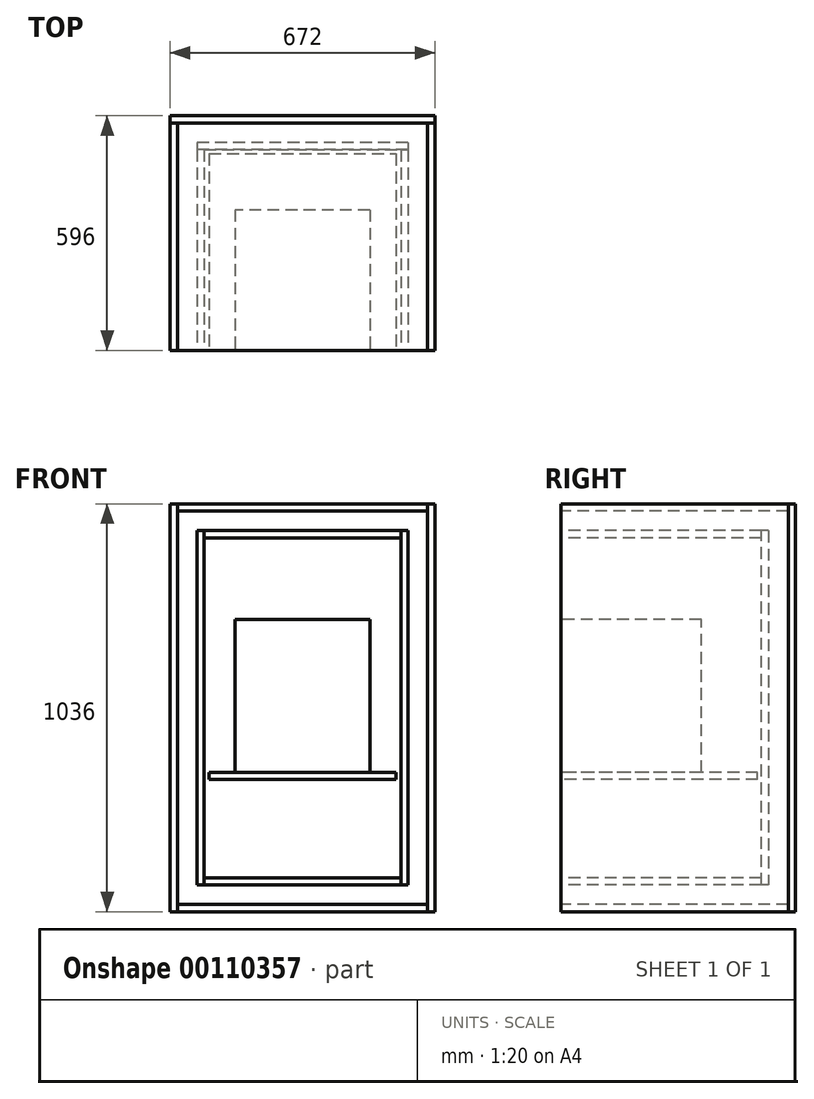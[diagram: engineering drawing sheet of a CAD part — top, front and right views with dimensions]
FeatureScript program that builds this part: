
annotation { "Feature Type Name" : "Feature", "Feature Type Description" : "" }
export const myFeature = defineFeature(function(context is Context, id is Id, definition is map)
    precondition{}
    {
        {
            var Q0;
            Q0=qCreatedBy(makeId("Front.planeOp"),FACE);
            var sketch = newSketch(context, id + "F0", { "sketchPlane" : qUnion([Q0])});
            skLineSegment(sketch, "E0.bottom", {"start": v(250, 0) * mm, "end": v(-250, 0) * mm});
            skLineSegment(sketch, "E0.top", {"start": v(250, 18) * mm, "end": v(-250, 18) * mm});
            skLineSegment(sketch, "E0.left", {"start": v(250, 0) * mm, "end": v(250, 18) * mm});
            skLineSegment(sketch, "E0.right", {"start": v(-250, 0) * mm, "end": v(-250, 18) * mm});
            skPoint(sketch, "E0.middle", {"position": v(0, 9) * mm});
            skLineSegment(sketch, "E1.bottom", {"start": v(-237.5, 268) * mm, "end": v(237.5, 268) * mm});
            skLineSegment(sketch, "E1.top", {"start": v(-237.5, 286) * mm, "end": v(237.5, 286) * mm});
            skLineSegment(sketch, "E1.left", {"start": v(-237.5, 268) * mm, "end": v(-237.5, 286) * mm});
            skLineSegment(sketch, "E1.right", {"start": v(237.5, 268) * mm, "end": v(237.5, 286) * mm});
            skLineSegment(sketch, "E2.bottom", {"start": v(250, 0) * mm, "end": v(268, 0) * mm});
            skLineSegment(sketch, "E2.top", {"start": v(250, 900) * mm, "end": v(268, 900) * mm});
            skLineSegment(sketch, "E2.left", {"start": v(250, 0) * mm, "end": v(250, 900) * mm});
            skLineSegment(sketch, "E2.right", {"start": v(268, 0) * mm, "end": v(268, 900) * mm});
            skLineSegment(sketch, "E3.MirrorCS", {"start": v(-250, 0) * mm, "end": v(-268, 0) * mm});
            skLineSegment(sketch, "E4.MirrorCS", {"start": v(-268, 0) * mm, "end": v(-268, 900) * mm});
            skLineSegment(sketch, "E5.MirrorCS", {"start": v(-250, 0) * mm, "end": v(-250, 900) * mm});
            skLineSegment(sketch, "E6.MirrorCS", {"start": v(-250, 900) * mm, "end": v(-268, 900) * mm});
            skLineSegment(sketch, "E7.bottom", {"start": v(-250, 900) * mm, "end": v(250, 900) * mm});
            skLineSegment(sketch, "E7.top", {"start": v(-250, 882) * mm, "end": v(250, 882) * mm});
            skLineSegment(sketch, "E7.left", {"start": v(-250, 900) * mm, "end": v(-250, 882) * mm});
            skLineSegment(sketch, "E7.right", {"start": v(250, 900) * mm, "end": v(250, 882) * mm});
            skLineSegment(sketch, "E8.bottom", {"start": v(-318, 968) * mm, "end": v(318, 968) * mm});
            skLineSegment(sketch, "E8.top", {"start": v(-318, 950) * mm, "end": v(318, 950) * mm});
            skLineSegment(sketch, "E8.left", {"start": v(-318, 968) * mm, "end": v(-318, 950) * mm});
            skLineSegment(sketch, "E8.right", {"start": v(318, 968) * mm, "end": v(318, 950) * mm});
            skLineSegment(sketch, "E9.bottom", {"start": v(-318, -50) * mm, "end": v(318, -50) * mm});
            skLineSegment(sketch, "E9.top", {"start": v(-318, -68) * mm, "end": v(318, -68) * mm});
            skLineSegment(sketch, "E9.left", {"start": v(-318, -50) * mm, "end": v(-318, -68) * mm});
            skLineSegment(sketch, "E9.right", {"start": v(318, -50) * mm, "end": v(318, -68) * mm});
            skLineSegment(sketch, "E10.bottom", {"start": v(318, 968) * mm, "end": v(336, 968) * mm});
            skLineSegment(sketch, "E10.top", {"start": v(318, -68) * mm, "end": v(336, -68) * mm});
            skLineSegment(sketch, "E10.left", {"start": v(318, 968) * mm, "end": v(318, -68) * mm});
            skLineSegment(sketch, "E10.right", {"start": v(336, 968) * mm, "end": v(336, -68) * mm});
            skLineSegment(sketch, "E11.bottom", {"start": v(-318, 968) * mm, "end": v(-336, 968) * mm});
            skLineSegment(sketch, "E11.top", {"start": v(-318, -68) * mm, "end": v(-336, -68) * mm});
            skLineSegment(sketch, "E11.left", {"start": v(-318, 968) * mm, "end": v(-318, -68) * mm});
            skLineSegment(sketch, "E11.right", {"start": v(-336, 968) * mm, "end": v(-336, -68) * mm});
            skLineSegment(sketch, "E12.bottom", {"start": v(-237.5, 286) * mm, "end": v(-219.5, 286) * mm});
            skLineSegment(sketch, "E12.top", {"start": v(-237.5, 386) * mm, "end": v(-219.5, 386) * mm});
            skLineSegment(sketch, "E12.left", {"start": v(-237.5, 286) * mm, "end": v(-237.5, 386) * mm});
            skLineSegment(sketch, "E12.right", {"start": v(-219.5, 286) * mm, "end": v(-219.5, 386) * mm});
            skLineSegment(sketch, "E13.bottom", {"start": v(237.5, 286) * mm, "end": v(219.5, 286) * mm});
            skLineSegment(sketch, "E13.top", {"start": v(237.5, 386) * mm, "end": v(219.5, 386) * mm});
            skLineSegment(sketch, "E13.left", {"start": v(237.5, 286) * mm, "end": v(237.5, 386) * mm});
            skLineSegment(sketch, "E13.right", {"start": v(219.5, 286) * mm, "end": v(219.5, 386) * mm});
            skSolve(sketch);
        }
        {
            var Q0;
            Q0=makeQuery(id+"F0.imprint","IMPRINT",FACE,{"disambiguationData":[TD([[makeQuery(id+"F0.imprint","IMPRINT",EDGE,{"derivedFrom":sQuery(id+"F0.wireOp",EDGE,"E0.bottom")}),-1.0]])]});
            extrude(context, id + "F1", {"entities" : qUnion([Q0]), "oppositeDirection" : true, "depth" : 510 * mm});
        }
        {
            var Q0;
            Q0=makeQuery(id+"F0.imprint","IMPRINT",FACE,{"disambiguationData":[TD([[makeQuery(id+"F0.imprint","IMPRINT",EDGE,{"derivedFrom":sQuery(id+"F0.wireOp",EDGE,"E1.top")}),-1.0]])]});
            extrude(context, id + "F2", {"entities" : qUnion([Q0]), "oppositeDirection" : true, "depth" : 500 * mm});
        }
        {
            var Q0;
            {var subQ3=sQuery(id+"F0.wireOp",EDGE,"E3.MirrorCS");Q0=makeQuery(id+"F0.imprint","IMPRINT",FACE,{"disambiguationData":[TD([[makeQuery(id+"F0.imprint","IMPRINT",EDGE,{"derivedFrom":subQ3}),-1.0]])]});}
            extrude(context, id + "F3", {"entities" : qUnion([Q0]), "oppositeDirection" : true, "depth" : 510 * mm});
        }
        {
            var Q0;
            {var subQ3=sQuery(id+"F0.wireOp",EDGE,"E2.bottom");Q0=makeQuery(id+"F0.imprint","IMPRINT",FACE,{"disambiguationData":[TD([[makeQuery(id+"F0.imprint","IMPRINT",EDGE,{"derivedFrom":subQ3}),1.0]])]});}
            extrude(context, id + "F4", {"entities" : qUnion([Q0]), "oppositeDirection" : true, "depth" : 510 * mm});
        }
        {
            var Q0;
            Q0=makeQuery(id+"F0.imprint","IMPRINT",FACE,{"disambiguationData":[TD([[makeQuery(id+"F0.imprint","IMPRINT",EDGE,{"derivedFrom":sQuery(id+"F0.wireOp",EDGE,"E7.bottom")}),-1.0]])]});
            extrude(context, id + "F5", {"entities" : qUnion([Q0]), "oppositeDirection" : true, "depth" : 510 * mm});
        }
        {
            var Q0;
            Q0=qCreatedBy(makeId("Front.planeOp"),FACE);
            var sketch = newSketch(context, id + "F6", { "sketchPlane" : qUnion([Q0])});
            skLineSegment(sketch, "E14.0", {"start": v(-237.5, 286) * mm, "end": v(237.5, 286) * mm, "construction": true});
            skLineSegment(sketch, "E15.bottom", {"start": v(171, 286) * mm, "end": v(-171, 286) * mm});
            skLineSegment(sketch, "E15.top", {"start": v(171, 674) * mm, "end": v(-171, 674) * mm});
            skLineSegment(sketch, "E15.left", {"start": v(171, 286) * mm, "end": v(171, 674) * mm});
            skLineSegment(sketch, "E15.right", {"start": v(-171, 286) * mm, "end": v(-171, 674) * mm});
            skPoint(sketch, "E15.middle", {"position": v(0, 480) * mm});
            skSolve(sketch);
        }
        {
            var Q0;
            Q0=makeQuery(id+"F6.imprint","IMPRINT",FACE,{"disambiguationData":[TD([[makeQuery(id+"F6.imprint","IMPRINT",EDGE,{"derivedFrom":sQuery(id+"F6.wireOp",EDGE,"E15.bottom")}),-1.0]])]});
            extrude(context, id + "F7", {"entities" : qUnion([Q0]), "oppositeDirection" : true, "depth" : 357 * mm});
        }
        {
            var Q0;
            Q0=makeQuery(id+"F5.opExtrude","CAP_FACE",FACE,{"disambiguationData":[OSD([sQuery(id+"F0.wireOp",EDGE,"E7.bottom"),sQuery(id+"F0.wireOp",EDGE,"E7.top"),sQuery(id+"F0.wireOp",EDGE,"E7.left"),sQuery(id+"F0.wireOp",EDGE,"E7.right")])],"isStart":false});
            var sketch = newSketch(context, id + "F8", { "sketchPlane" : qUnion([Q0])});
            skLineSegment(sketch, "E16.0", {"start": v(-268, 0) * mm, "end": v(-268, 900) * mm, "construction": true});
            skLineSegment(sketch, "E17.0", {"start": v(268, 0) * mm, "end": v(268, 900) * mm, "construction": true});
            skLineSegment(sketch, "E18.bottom", {"start": v(-268, 900) * mm, "end": v(268, 900) * mm});
            skLineSegment(sketch, "E18.top", {"start": v(-268, 0) * mm, "end": v(268, 0) * mm});
            skLineSegment(sketch, "E18.left", {"start": v(-268, 900) * mm, "end": v(-268, 0) * mm});
            skLineSegment(sketch, "E18.right", {"start": v(268, 900) * mm, "end": v(268, 0) * mm});
            skSolve(sketch);
        }
        {
            var Q0;
            Q0 = qSketchRegion(id + "F8", true);
            extrude(context, id + "F9", {"entities" : qUnion([Q0]), "depth" : 18 * mm});
        }
        {
            var Q0;
            {var subQ3=sQuery(id+"F0.wireOp",EDGE,"E11.bottom");Q0=makeQuery(id+"F0.imprint","IMPRINT",FACE,{"disambiguationData":[TD([[makeQuery(id+"F0.imprint","IMPRINT",EDGE,{"derivedFrom":subQ3}),1.0]])]});}
            extrude(context, id + "F10", {"entities" : qUnion([Q0]), "oppositeDirection" : true, "depth" : (510 + 50 + 18) * mm});
        }
        {
            var Q0;
            {var subQ0=sQuery(id+"F0.wireOp",EDGE,"E8.bottom");Q0=makeQuery(id+"F0.imprint","IMPRINT",FACE,{"disambiguationData":[TD([[makeQuery(id+"F0.imprint","IMPRINT",EDGE,{"derivedFrom":subQ0}),-1.0]])]});}
            extrude(context, id + "F11", {"entities" : qUnion([Q0]), "oppositeDirection" : true, "depth" : (510 + 18 + 50) * mm});
        }
        {
            var Q0;
            {var subQ0=sQuery(id+"F0.wireOp",EDGE,"E9.bottom");Q0=makeQuery(id+"F0.imprint","IMPRINT",FACE,{"disambiguationData":[TD([[makeQuery(id+"F0.imprint","IMPRINT",EDGE,{"derivedFrom":subQ0}),-1.0]])]});}
            extrude(context, id + "F12", {"entities" : qUnion([Q0]), "oppositeDirection" : true, "depth" : (510 + 18 + 50) * mm});
        }
        {
            var Q0;
            {var subQ3=sQuery(id+"F0.wireOp",EDGE,"E10.bottom");Q0=makeQuery(id+"F0.imprint","IMPRINT",FACE,{"disambiguationData":[TD([[makeQuery(id+"F0.imprint","IMPRINT",EDGE,{"derivedFrom":subQ3}),-1.0]])]});}
            extrude(context, id + "F13", {"entities" : qUnion([Q0]), "oppositeDirection" : true, "depth" : (510 + 18 + 50) * mm});
        }
        {
            var Q0;
            Q0=makeQuery(id+"F11.opExtrude","CAP_FACE",FACE,{"disambiguationData":[OSD([sQuery(id+"F0.wireOp",EDGE,"E8.bottom"),sQuery(id+"F0.wireOp",EDGE,"E8.top"),sQuery(id+"F0.wireOp",EDGE,"E10.left"),sQuery(id+"F0.wireOp",EDGE,"E11.left")])],"isStart":false});
            var sketch = newSketch(context, id + "F14", { "sketchPlane" : qUnion([Q0])});
            skLineSegment(sketch, "E19.0", {"start": v(-336, 968) * mm, "end": v(-336, -68) * mm, "construction": true});
            skLineSegment(sketch, "E19.1", {"start": v(336, 968) * mm, "end": v(336, -68) * mm, "construction": true});
            skLineSegment(sketch, "E20.bottom", {"start": v(-336, 968) * mm, "end": v(336, 968) * mm});
            skLineSegment(sketch, "E20.top", {"start": v(-336, -68) * mm, "end": v(336, -68) * mm});
            skLineSegment(sketch, "E20.left", {"start": v(-336, 968) * mm, "end": v(-336, -68) * mm});
            skLineSegment(sketch, "E20.right", {"start": v(336, 968) * mm, "end": v(336, -68) * mm});
            skSolve(sketch);
        }
        {
            var Q0;
            Q0 = qSketchRegion(id + "F14", true);
            extrude(context, id + "F15", {"entities" : qUnion([Q0]), "depth" : 18 * mm});
        }
    });
